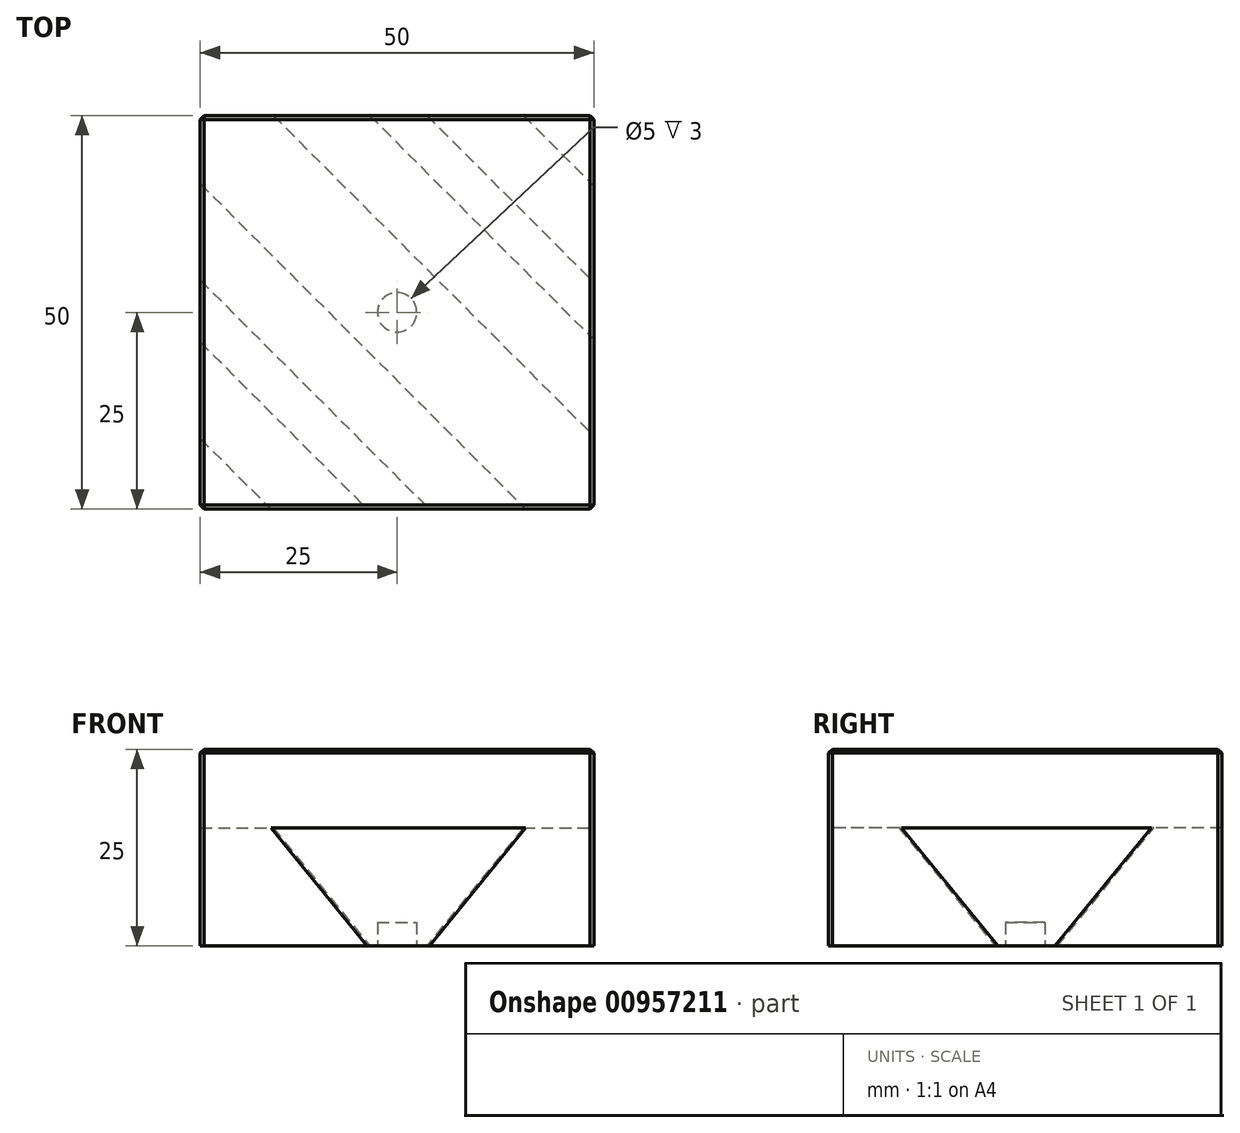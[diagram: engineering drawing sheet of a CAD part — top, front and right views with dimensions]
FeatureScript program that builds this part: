
annotation { "Feature Type Name" : "Feature", "Feature Type Description" : "" }
export const myFeature = defineFeature(function(context is Context, id is Id, definition is map)
    precondition{}
    {
        {
            var Q0;
            Q0=qCreatedBy(makeId("Top.planeOp"),FACE);
            var sketch = newSketch(context, id + "F0", { "sketchPlane" : qUnion([Q0])});
            skLineSegment(sketch, "E0.bottom", {"start": v(25, 25) * mm, "end": v(-25, 25) * mm});
            skLineSegment(sketch, "E0.top", {"start": v(25, -25) * mm, "end": v(-25, -25) * mm});
            skLineSegment(sketch, "E0.left", {"start": v(25, 25) * mm, "end": v(25, -25) * mm});
            skLineSegment(sketch, "E0.right", {"start": v(-25, 25) * mm, "end": v(-25, -25) * mm});
            skPoint(sketch, "E0.middle", {"position": v(0, 0) * mm});
            skSolve(sketch);
        }
        {
            var Q0;
            Q0=makeQuery(id+"F0.imprint","IMPRINT",FACE,{"disambiguationData":[TD([[makeQuery(id+"F0.imprint","IMPRINT",EDGE,{"derivedFrom":sQuery(id+"F0.wireOp",EDGE,"E0.bottom")}),1.0]])]});
            extrude(context, id + "F1", {"entities" : qUnion([Q0]), "depth" : 25 * mm, "offsetDistance" : 25 * mm});
        }
        {
            var Q0;
            Q0=makeQuery(id+"F1.opExtrude","SWEPT_EDGE",EDGE,{"disambiguationData":[OSD([sQuery(id+"F0.wireOp",EDGE,"E0.top"),sQuery(id+"F0.wireOp",EDGE,"E0.left")])]});
            cPlane(context, id + "F2", {"entities" : qUnion([Q0]), "cplaneType" : CPlaneType.LINE_ANGLE, "offset" : 25 * mm, "angle" : 45 * degree, "width" : 150 * mm, "height" : 150 * mm});
        }
        {
            var Q0;
            Q0=qCreatedBy(id+"F2.planeOp",FACE);
            var sketch = newSketch(context, id + "F3", { "sketchPlane" : qUnion([Q0])});
            skLineSegment(sketch, "E1.0", {"start": v(0, 25) * mm, "end": v(35.36, 25) * mm});
            skLineSegment(sketch, "E2.0", {"start": v(-35.36, 25) * mm, "end": v(0, 25) * mm});
            skLineSegment(sketch, "E3.0", {"start": v(35.36, 25) * mm, "end": v(35.36, 0) * mm});
            skLineSegment(sketch, "E4.0", {"start": v(-35.36, 25) * mm, "end": v(-35.36, 0) * mm});
            skLineSegment(sketch, "E5", {"start": v(29.02, 25) * mm, "end": v(20.36, 10) * mm});
            skLineSegment(sketch, "E6", {"start": v(20.36, 10) * mm, "end": v(35.36, 10) * mm});
            skLineSegment(sketch, "E7.MirrorCS", {"start": v(-29.02, 25) * mm, "end": v(-20.36, 10) * mm});
            skLineSegment(sketch, "E8.MirrorCS", {"start": v(-20.36, 10) * mm, "end": v(-35.36, 10) * mm});
            skLineSegment(sketch, "E9", {"start": v(-6.56, 25) * mm, "end": v(-15.22, 10) * mm});
            skLineSegment(sketch, "E10", {"start": v(-15.22, 10) * mm, "end": v(14.78, 10) * mm});
            skLineSegment(sketch, "E11", {"start": v(14.78, 10) * mm, "end": v(6.12, 25) * mm});
            skPoint(sketch, "E12.endSnap0", {"position": v(-0.22, 10) * mm});
            skSolve(sketch);
        }
        {
            var Q0;
            {var subQ3=sQuery(id+"F3.wireOp",EDGE,"E5");Q0=makeQuery(id+"F3.imprint","IMPRINT",FACE,{"disambiguationData":[TD([[makeQuery(id+"F3.imprint","IMPRINT",EDGE,{"derivedFrom":subQ3}),1.0]])]});}
            var Q1;
            {var subQ3=sQuery(id+"F3.wireOp",EDGE,"E7.MirrorCS");Q1=makeQuery(id+"F3.imprint","IMPRINT",FACE,{"disambiguationData":[TD([[makeQuery(id+"F3.imprint","IMPRINT",EDGE,{"derivedFrom":subQ3}),-1.0]])]});}
            var Q2;
            {var subQ4=sQuery(id+"F3.wireOp",EDGE,"E9");Q2=makeQuery(id+"F3.imprint","IMPRINT",FACE,{"disambiguationData":[TD([[makeQuery(id+"F3.imprint","IMPRINT",EDGE,{"derivedFrom":subQ4}),1.0]])]});}
            extrude(context, id + "F4", {"entities" : qUnion([Q0, Q1, Q2]), "operationType" : NewBodyOperationType.REMOVE, "endBound" : BoundingType.THROUGH_ALL, "depth" : 25 * mm, "offsetDistance" : 25 * mm});
        }
        {
            var Q0;
            Q0=makeQuery(id+"F4.boolean.opBoolean","COPY",FACE,{"derivedFrom":makeQuery(id+"F4.opExtrude","SWEPT_FACE",FACE,{"disambiguationData":[OSD([sQuery(id+"F3.wireOp",EDGE,"E10")])]})});
            var sketch = newSketch(context, id + "F5", { "sketchPlane" : qUnion([Q0])});
            skPoint(sketch, "E13.0", {"position": v(-25, -25) * mm});
            skPoint(sketch, "E14.0", {"position": v(25, 25) * mm});
            skLineSegment(sketch, "E15.bottom", {"start": v(-25, -25) * mm, "end": v(25, -25) * mm});
            skLineSegment(sketch, "E15.top", {"start": v(-25, 25) * mm, "end": v(25, 25) * mm});
            skLineSegment(sketch, "E15.left", {"start": v(-25, -25) * mm, "end": v(-25, 25) * mm});
            skLineSegment(sketch, "E15.right", {"start": v(25, -25) * mm, "end": v(25, 25) * mm});
            skSolve(sketch);
        }
        {
            var Q0;
            Q0=qSketchRegion(id+"F5",true);
            extrude(context, id + "F6", {"entities" : qUnion([Q0]), "depth" : 25 * mm, "offsetDistance" : 25 * mm});
        }
        {
            var Q0;
            Q0=makeQuery(id+"F1.opExtrude","SWEPT_BODY",BODY,{"disambiguationData":[OSD([sQuery(id+"F0.wireOp",EDGE,"E0.bottom"),sQuery(id+"F0.wireOp",EDGE,"E0.top"),sQuery(id+"F0.wireOp",EDGE,"E0.left"),sQuery(id+"F0.wireOp",EDGE,"E0.right")])]});
            var Q1;
            Q1=makeQuery(id+"F6.opExtrude","SWEPT_BODY",BODY,{"disambiguationData":[OSD([sQuery(id+"F5.wireOp",EDGE,"E15.bottom"),sQuery(id+"F5.wireOp",EDGE,"E15.top"),sQuery(id+"F5.wireOp",EDGE,"E15.left"),sQuery(id+"F5.wireOp",EDGE,"E15.right")])]});
            booleanBodies(context, id + "F7", {"operationType" : BooleanOperationType.SUBTRACTION, "tools" : qUnion([Q0]), "targets" : qUnion([Q1]), "keepTools" : true});
        }
        {
            var Q0;
            Q0=makeQuery(id+"F6.opExtrude","SWEPT_BODY",BODY,{"disambiguationData":[OSD([sQuery(id+"F5.wireOp",EDGE,"E15.bottom"),sQuery(id+"F5.wireOp",EDGE,"E15.top"),sQuery(id+"F5.wireOp",EDGE,"E15.left"),sQuery(id+"F5.wireOp",EDGE,"E15.right")])]});
            var Q1;
            Q1=makeQuery(id+"F1.opExtrude","CAP_EDGE",EDGE,{"disambiguationData":[OSD([sQuery(id+"F0.wireOp",EDGE,"E0.top")])],"isStart":true});
            transform(context, id + "F8", {"entities" : qUnion([Q0]), "transformType" : TransformType.TRANSLATION_DISTANCE, "transformDirection" : qUnion([Q1]), "distance" : 55 * mm, "makeCopy" : false});
        }
        {
            var Q0;
            Q0=makeQuery(id+"F6.opExtrude","SWEPT_EDGE",EDGE,{"disambiguationData":[OSD([sQuery(id+"F5.wireOp",EDGE,"E15.top"),sQuery(id+"F5.wireOp",EDGE,"E15.left")])]});
            var Q1;
            Q1=makeQuery(id+"F6.opExtrude","SWEPT_EDGE",EDGE,{"disambiguationData":[OSD([sQuery(id+"F5.wireOp",EDGE,"E15.bottom"),sQuery(id+"F5.wireOp",EDGE,"E15.left")])]});
            var Q2;
            Q2=makeQuery(id+"F6.opExtrude","SWEPT_EDGE",EDGE,{"disambiguationData":[OSD([sQuery(id+"F5.wireOp",EDGE,"E15.top"),sQuery(id+"F5.wireOp",EDGE,"E15.right")])]});
            var Q3;
            Q3=makeQuery(id+"F6.opExtrude","SWEPT_EDGE",EDGE,{"disambiguationData":[OSD([sQuery(id+"F5.wireOp",EDGE,"E15.bottom"),sQuery(id+"F5.wireOp",EDGE,"E15.right")])]});
            var Q4;
            Q4=makeQuery(id+"F6.opExtrude","CAP_EDGE",EDGE,{"disambiguationData":[OSD([sQuery(id+"F5.wireOp",EDGE,"E15.right")])],"isStart":false});
            var Q5;
            Q5=makeQuery(id+"F6.opExtrude","CAP_EDGE",EDGE,{"disambiguationData":[OSD([sQuery(id+"F5.wireOp",EDGE,"E15.top")])],"isStart":false});
            var Q6;
            Q6=makeQuery(id+"F6.opExtrude","CAP_EDGE",EDGE,{"disambiguationData":[OSD([sQuery(id+"F5.wireOp",EDGE,"E15.left")])],"isStart":false});
            var Q7;
            Q7=makeQuery(id+"F6.opExtrude","CAP_EDGE",EDGE,{"disambiguationData":[OSD([sQuery(id+"F5.wireOp",EDGE,"E15.bottom")])],"isStart":false});
            chamfer(context, id + "F9", {"entities" : qUnion([Q0, Q1, Q2, Q3, Q4, Q5, Q6, Q7]), "width" : .5 * mm, "tangentPropagation" : true});
        }
        {
            var Q0;
            Q0=makeQuery(id+"F1.opExtrude","SWEPT_BODY",BODY,{"disambiguationData":[OSD([sQuery(id+"F0.wireOp",EDGE,"E0.bottom"),sQuery(id+"F0.wireOp",EDGE,"E0.top"),sQuery(id+"F0.wireOp",EDGE,"E0.left"),sQuery(id+"F0.wireOp",EDGE,"E0.right")])]});
            deleteBodies(context, id + "F10", {"entities" : qUnion([Q0])});
        }
        {
            var Q0;
            {var subQ0=sQuery(id+"F5.wireOp",EDGE,"E15.bottom");var subQ1=sQuery(id+"F5.wireOp",EDGE,"E15.top");var subQ2=sQuery(id+"F5.wireOp",EDGE,"E15.right");var subQ3=sQuery(id+"F5.wireOp",EDGE,"E15.left");Q0=makeQuery(id+"F7.opBoolean","SPLIT",FACE,{"disambiguationData":[TD([makeQuery(id+"F4.boolean.opBoolean","COPY",FACE,{"derivedFrom":makeQuery(id+"F4.opExtrude","SWEPT_FACE",FACE,{"disambiguationData":[OSD([sQuery(id+"F3.wireOp",EDGE,"E9")])]})})])],"derivedFrom":makeQuery(id+"F6.opExtrude","CAP_FACE",FACE,{"disambiguationData":[OSD([subQ0,subQ1,subQ3,subQ2])],"isStart":true})});}
            var sketch = newSketch(context, id + "F11", { "sketchPlane" : qUnion([Q0])});
            skLineSegment(sketch, "E16", {"start": v(-79.75, -24.75) * mm, "end": v(-30.25, 24.75) * mm, "construction": true});
            skPoint(sketch, "E17.0", {"position": v(-30.25, -24.75) * mm});
            skPoint(sketch, "E18.0", {"position": v(-79.75, 24.75) * mm});
            skLineSegment(sketch, "E19", {"start": v(-79.75, 24.75) * mm, "end": v(-30.25, -24.75) * mm, "construction": true});
            skCircle(sketch, "E20", {"center": v(-55, 0) * mm, "radius": 2.5 * mm});
            skSolve(sketch);
        }
        {
            var Q0;
            Q0 = qSketchRegion(id + "F11", true);
            extrude(context, id + "F12", {"entities" : qUnion([Q0]), "operationType" : NewBodyOperationType.REMOVE, "oppositeDirection" : true, "depth" : 3 * mm, "offsetDistance" : 25 * mm});
        }
    });
